# Revit family: Door-Automatic_Slide-Nabco-Bipart-Full_Open-Hurricane
name_source: partatom
category: Doors
revit_build: Autodesk Revit MEP 2012 (Build: 20110916_2132(x64)
units: mm (PartAtom-declared; Revit-internal decimal feet)

## types (3) — shared parameters
Date Last Modified = March 10, 2015
Description = See Part Description
Equipment Abbreviation = ASD
Family Version = 1.0
Function = Exterior
Manufacturer = NABCO Entrances Inc.
Model = See Part Number
Model Disclaimer = This model represents a highly customizable product.  Contact NABCO Entrances Inc. for more information
Product Documentation Link = http://www.nabcoentrances.com
Show Arrows = No
Thickness = 1.75 "
URL = http://www.nabcoentrances.com

## per-type parameters (varying)
| type | zz Integer 1 | zz Integer 2 | zz Length 3 | zz Length 7 |
| H60, Narrow Stile | 1 | 60 | 2.25 " | 1.125 " |
| H60, Medium Stile | 2 | 60 | 4 " | 2 " |
| H105, Medium Stile | 2 | 105 | 4 " | 2 " |

## geometry (parser evidence)
native form markers: Blend x2, Sweep x7
no freeform markers — native parametric forms only
